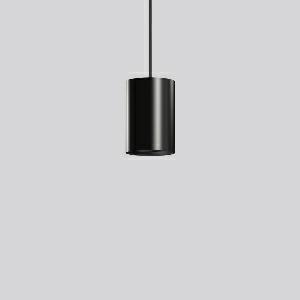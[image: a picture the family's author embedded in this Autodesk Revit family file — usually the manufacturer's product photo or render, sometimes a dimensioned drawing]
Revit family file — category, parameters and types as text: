
# Revit family: deecos_p_maxi_911536_003_76_3270
name_source: partatom
category: Lighting Fixtures
units: mm (PartAtom-declared; Revit-internal decimal feet)

## family parameters
Cut with Voids When Loaded = No
Host = Face
Light Source = No
Part Type = Normal
Room Calculation Point = No
Round Connector Dimension = Use Diameter
Shared = No

## types (1)
- DEECOS P maxi (1 x LED Modul 930, 4200 lm, 3000)
    Apparent Load = 35 VA
    Approval mark = CE
    CIE Flux Codes = 100 100 100 100 100
    Color Rendering = 90
    Color Temperature = 3000
    Default Elevation = 1800 mm
    Description = Series: DEECOS P maxi
Cylindrical pendant luminaire. Housing: die-cast aluminium, powder-coated. Canopy made of powder-coated sheet steel with magnetic attachment. Optical assembly with reflector made of MIRO-Silver with 98% total light reflection for outstanding efficiency - can be changed without tools. Best colour rendering index Ra>90. Transparent suspension cable 2 m, can be shortened. High quality converter without flickering and stroboscopic effect. The following accessories can be mounted without use of tools: interchangeable lenses, honeycomb louvre, clear and frosted diffusers, white interchangeable plastic ring. Decorative recessed suspension set available as accessory. 
Colour: deep black, matt (RAL 9005)
Diameter: 123 mm
Height: 181 mm
Suspension length: 2000 mm
Lamp: LED
Socket: without socket
Colour temperature: 3000K
Colour rendering index (CRI): 92
System power: 35 W
Rated luminous flux: 4200 lm
Luminous efficiency: 120 lm/W
Control gear: Converter, dimmable, DALI
Protection class: I
Type of protection: IP 20
    Height = 181 mm
    Lamp = 1 x LED Modul 930
    Lamp Light Flux = 4200 lm
    Lamp count = 1
    Length = 123 mm
    Lifetime = 50000 h
    Luminous efficacy = 120 lm/W
    Manufacturer = RZB
    ModVariant = No
    Model = 911536.003.76
    Mounting Place = Ceiling
    Mounting Type = Pendant
    Number of Poles = 1
    OnlyDefault = Yes
    Power Factor = 1
    Product Name = DEECOS P maxi
    Product group = Pendant luminaires
    ProductGroupID = 902
    Protection Class = Protection class I
    Protection Degree = IP 20
    RLX_Detail_Level = 1
    RLX_Emergency_Light_Flux = 0 lm
    RLX_Emergency_Type = 0
    RLX_Emergency_Type_DB = No
    RlxData = <blob elided: 36433 chars, md5=37e8ecf5>
    Socket = socket
    Standby Power = 0 W
    System Light Flux = 4200 lm
    System Power = 35 W
    Type Comments = Product without accessories
    Type Image = 911480.003.jpg
    URL = http://relux.com
    VarID = ---
    Voltage = 230 V
    Voltage Range = 220-240 V
    Weight = 0.00 kg
    Width = 0 mm  [stored 0 ft]

note: [stored X ft] marks values corroborated as IEEE doubles in the binary element streams (Revit-internal decimal feet)

## geometry (parser evidence)
native form markers: Blend x4, Sweep x9
no freeform markers — native parametric forms only
